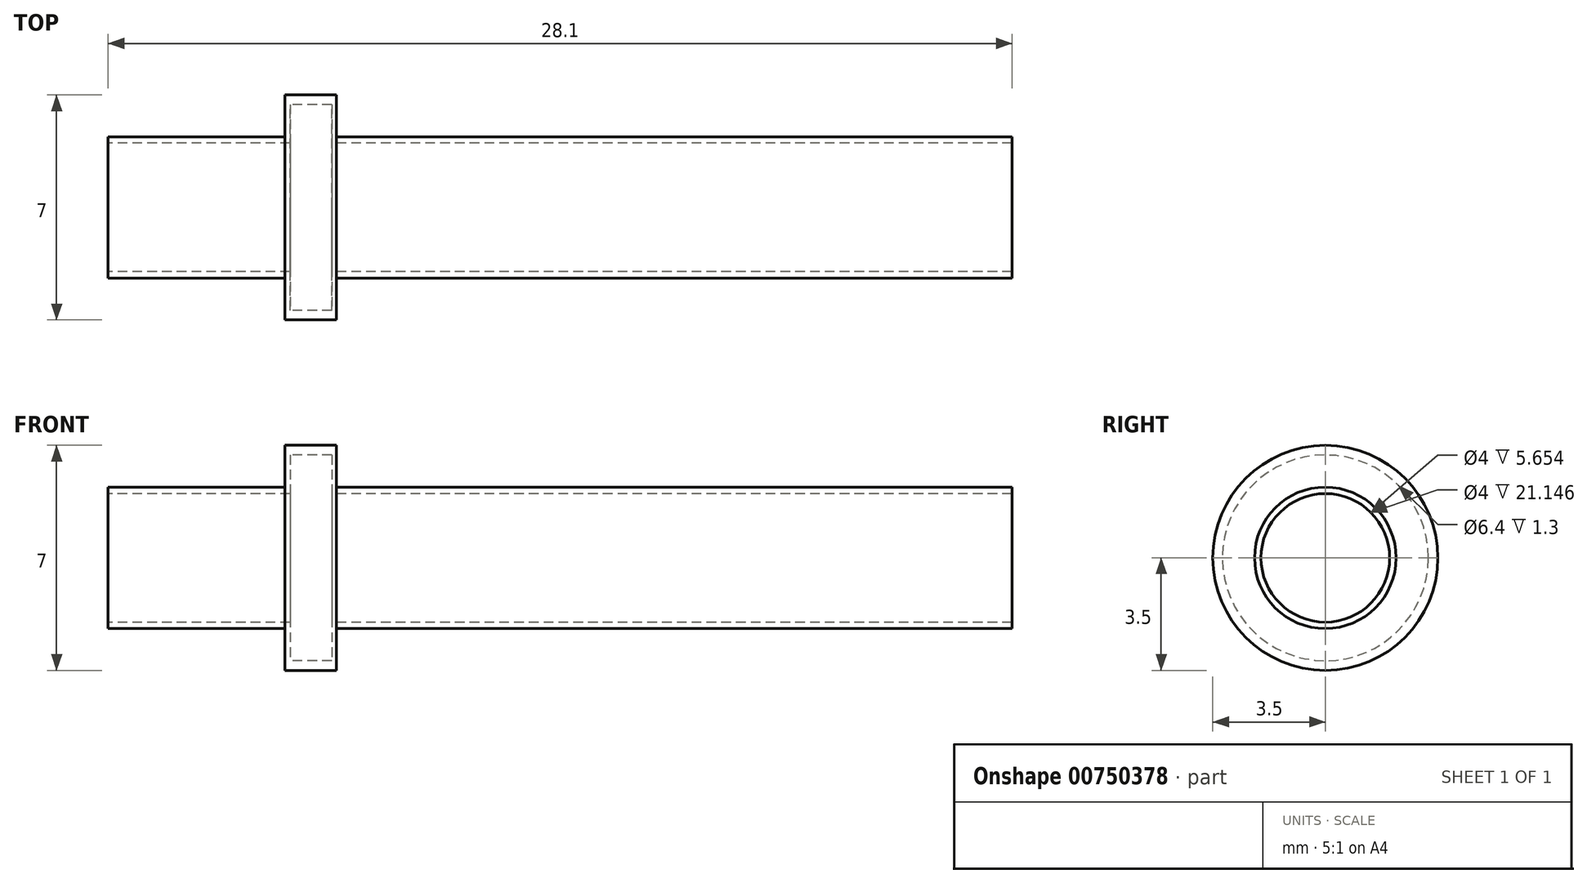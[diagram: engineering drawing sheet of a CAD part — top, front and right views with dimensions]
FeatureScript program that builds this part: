
annotation { "Feature Type Name" : "Feature", "Feature Type Description" : "" }
export const myFeature = defineFeature(function(context is Context, id is Id, definition is map)
    precondition{}
    {
        {
            var Q0;
            Q0=qCreatedBy(makeId("Front.planeOp"),FACE);
            var sketch = newSketch(context, id + "F0", { "sketchPlane" : qUnion([Q0])});
            skLineSegment(sketch, "E0", {"start": v(-19.12, 2.2) * mm, "end": v(-13.62, 2.2) * mm});
            skLineSegment(sketch, "E1", {"start": v(-13.62, 2.2) * mm, "end": v(-13.62, 3.5) * mm});
            skLineSegment(sketch, "E2", {"start": v(-13.62, 3.5) * mm, "end": v(-12.02, 3.5) * mm});
            skLineSegment(sketch, "E3", {"start": v(-12.02, 3.5) * mm, "end": v(-12.02, 2.2) * mm});
            skLineSegment(sketch, "E4", {"start": v(-12.02, 2.2) * mm, "end": v(8.98, 2.2) * mm});
            skLineSegment(sketch, "E5", {"start": v(8.98, 2.2) * mm, "end": v(8.98, 0) * mm});
            skLineSegment(sketch, "E6", {"start": v(-19.12, 0) * mm, "end": v(-19.12, 2.2) * mm});
            skLineSegment(sketch, "E7", {"start": v(-23.58, 0) * mm, "end": v(15.51, 0) * mm});
            skSolve(sketch);
        }
        {
            var Q0;
            Q0=makeQuery(id+"F0.imprint","IMPRINT",FACE,{"disambiguationData":[TD([[makeQuery(id+"F0.imprint","IMPRINT",EDGE,{"derivedFrom":sQuery(id+"F0.wireOp",EDGE,"E0")}),-1.0]])]});
            var Q1;
            Q1=sQuery(id+"F0.wireOp",EDGE,"E7");
            revolve(context, id + "F1", {"surfaceOperationType" : NewSurfaceOperationType.NEW, "entities" : qUnion([Q0]), "axis" : qUnion([Q1]), "revolveType" : RevolveType.FULL});
        }
        {
            var Q0;
            Q0=qCreatedBy(makeId("Front.planeOp"),FACE);
            var sketch = newSketch(context, id + "F2", { "sketchPlane" : qUnion([Q0])});
            skLineSegment(sketch, "E8", {"start": v(-19.47, 2) * mm, "end": v(-13.47, 2) * mm});
            skLineSegment(sketch, "E9", {"start": v(-13.47, 2) * mm, "end": v(-13.47, 3.2) * mm});
            skLineSegment(sketch, "E10", {"start": v(-13.47, 3.2) * mm, "end": v(-12.17, 3.2) * mm});
            skLineSegment(sketch, "E11", {"start": v(-12.17, 3.2) * mm, "end": v(-12.17, 2) * mm});
            skLineSegment(sketch, "E12", {"start": v(-12.17, 2) * mm, "end": v(10.83, 2) * mm});
            skLineSegment(sketch, "E13", {"start": v(10.83, 2) * mm, "end": v(10.83, 0) * mm});
            skLineSegment(sketch, "E14", {"start": v(10.83, 0) * mm, "end": v(-20.48, 0) * mm});
            skLineSegment(sketch, "E15", {"start": v(-19.47, 2) * mm, "end": v(-19.47, 0) * mm});
            skSolve(sketch);
        }
        {
            var Q0;
            Q0 = qSketchRegion(id + "F2", true);
            var Q1;
            Q1=sQuery(id+"F2.wireOp",EDGE,"E14");
            revolve(context, id + "F3", {"operationType" : NewBodyOperationType.REMOVE, "surfaceOperationType" : NewSurfaceOperationType.NEW, "entities" : qUnion([Q0]), "axis" : qUnion([Q1]), "revolveType" : RevolveType.FULL, "oppositeDirection" : true});
        }
    });
